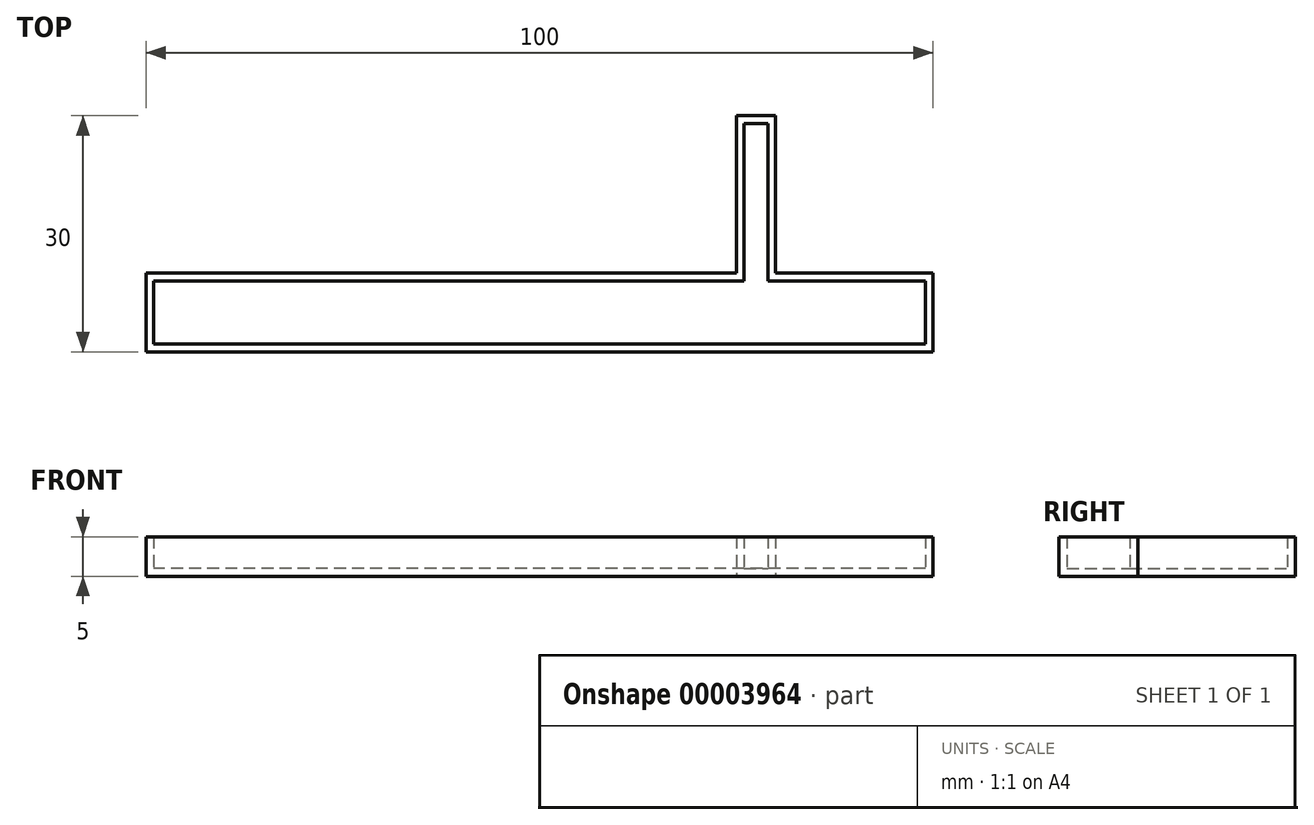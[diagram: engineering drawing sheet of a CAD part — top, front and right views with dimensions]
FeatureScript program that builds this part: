
annotation { "Feature Type Name" : "Feature", "Feature Type Description" : "" }
export const myFeature = defineFeature(function(context is Context, id is Id, definition is map)
    precondition{}
    {
        {
            var Q0;
            Q0=qCreatedBy(makeId("Top.planeOp"),FACE);
            var sketch = newSketch(context, id + "F0", { "sketchPlane" : qUnion([Q0])});
            skLineSegment(sketch, "E0.rect.bottom", {"start": v(50, -5) * mm, "end": v(-50, -5) * mm});
            skLineSegment(sketch, "E0.rect.top", {"start": v(50, 5) * mm, "end": v(-50, 5) * mm});
            skLineSegment(sketch, "E0.rect.left", {"start": v(50, -5) * mm, "end": v(50, 5) * mm});
            skLineSegment(sketch, "E0.rect.right", {"start": v(-50, -5) * mm, "end": v(-50, 5) * mm});
            skPoint(sketch, "E0.rect.middle", {"position": v(0, 0) * mm});
            skLineSegment(sketch, "E1", {"start": v(-50, 5) * mm, "end": v(0, 5) * mm, "construction": true});
            skLineSegment(sketch, "E2.bottom", {"start": v(-25, 5) * mm, "end": v(-30, 5) * mm});
            skLineSegment(sketch, "E2.top", {"start": v(-25, 25) * mm, "end": v(-30, 25) * mm});
            skLineSegment(sketch, "E2.left", {"start": v(-25, 5) * mm, "end": v(-25, 25) * mm});
            skLineSegment(sketch, "E2.right", {"start": v(-30, 5) * mm, "end": v(-30, 25) * mm});
            skLineSegment(sketch, "E3.0.MirrorCS", {"start": v(25, 25) * mm, "end": v(30, 25) * mm});
            skLineSegment(sketch, "E4.0.MirrorCS", {"start": v(30, 5) * mm, "end": v(30, 25) * mm});
            skLineSegment(sketch, "E5.0.MirrorCS", {"start": v(25, 5) * mm, "end": v(25, 25) * mm});
            skSolve(sketch);
        }
        {
            var Q0;
            Q0=makeQuery(id+"F0.imprint","IMPRINT",FACE,{"disambiguationData":[TD([[makeQuery(id+"F0.imprint","IMPRINT",EDGE,{"derivedFrom":sQuery(id+"F0.wireOp",EDGE,"E0.rect.bottom")}),-1.0]])]});
            var Q1;
            Q1=makeQuery(id+"F0.imprint","IMPRINT",FACE,{"disambiguationData":[TD([[makeQuery(id+"F0.imprint","IMPRINT",EDGE,{"derivedFrom":sQuery(id+"F0.wireOp",EDGE,"E2.bottom")}),-1.0]])]});
            var Q2;
            Q2=makeQuery(id+"F0.imprint","IMPRINT",FACE,{"disambiguationData":[TD([[makeQuery(id+"F0.imprint","IMPRINT",EDGE,{"derivedFrom":sQuery(id+"F0.wireOp",EDGE,"E3.0.MirrorCS")}),-1.0]])]});
            extrude(context, id + "F1", {"entities" : qUnion([Q0, Q1, Q2]), "depth" : 5 * mm});
        }
        {
            var Q0;
            Q0=makeQuery(id+"F1.opExtrude","CAP_FACE",FACE,{"disambiguationData":[OSD([sQuery(id+"F0.wireOp",EDGE,"E0.rect.bottom"),sQuery(id+"F0.wireOp",EDGE,"E0.rect.top"),sQuery(id+"F0.wireOp",EDGE,"E0.rect.left"),sQuery(id+"F0.wireOp",EDGE,"E0.rect.right"),sQuery(id+"F0.wireOp",EDGE,"E2.top"),sQuery(id+"F0.wireOp",EDGE,"E2.left"),sQuery(id+"F0.wireOp",EDGE,"E2.right"),sQuery(id+"F0.wireOp",EDGE,"E3.0.MirrorCS"),sQuery(id+"F0.wireOp",EDGE,"E4.0.MirrorCS"),sQuery(id+"F0.wireOp",EDGE,"E5.0.MirrorCS")])],"isStart":false});
            shell(context, id + "F2", {"entities" : qUnion([Q0]), "thickness" : 1 * mm});
        }
    });
